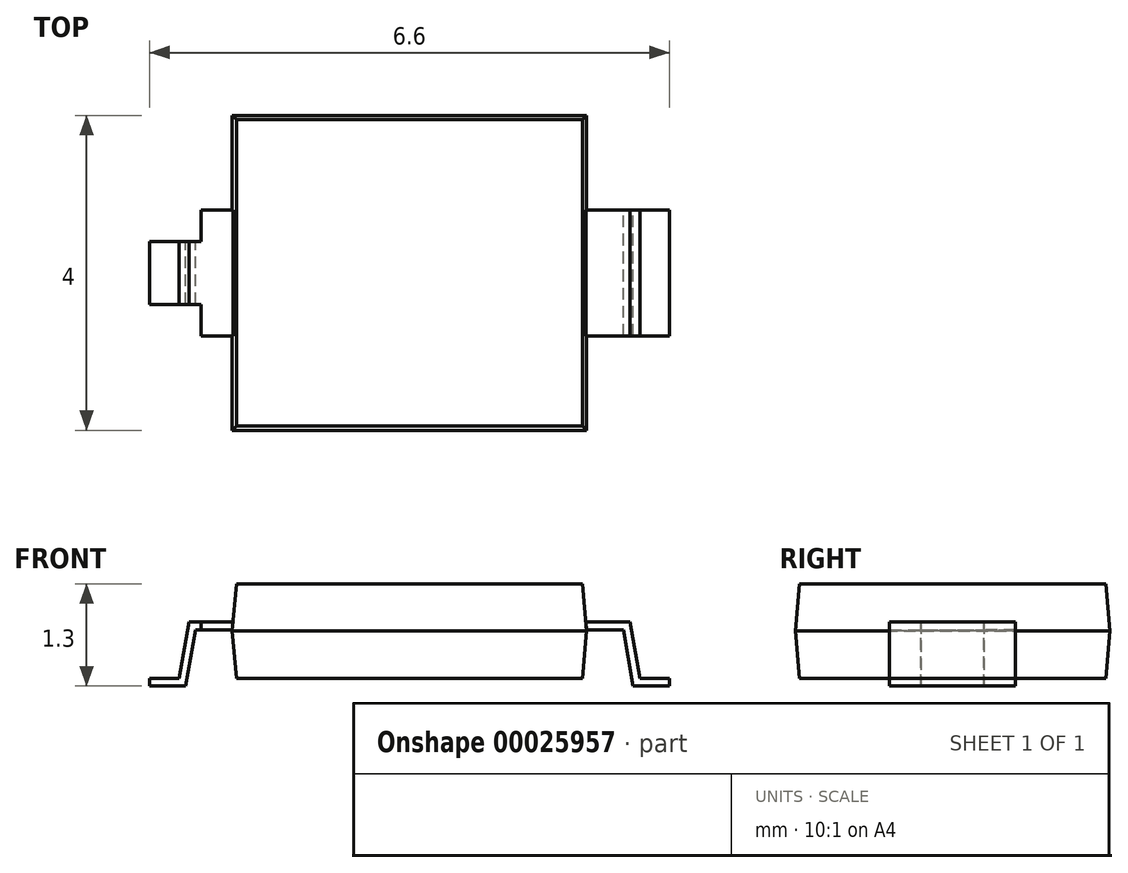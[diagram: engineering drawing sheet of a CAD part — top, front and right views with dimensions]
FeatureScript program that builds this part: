
annotation { "Feature Type Name" : "Feature", "Feature Type Description" : "" }
export const myFeature = defineFeature(function(context is Context, id is Id, definition is map)
    precondition{}
    {
        {
            var Q0;
            Q0=qCreatedBy(makeId("Top.planeOp"),FACE);
            var sketch = newSketch(context, id + "F0", { "sketchPlane" : qUnion([Q0])});
            skLineSegment(sketch, "E0.rect.bottom", {"start": v(2.25, -2) * mm, "end": v(-2.25, -2) * mm});
            skLineSegment(sketch, "E0.rect.top", {"start": v(2.25, 2) * mm, "end": v(-2.25, 2) * mm});
            skLineSegment(sketch, "E0.rect.left", {"start": v(2.25, -2) * mm, "end": v(2.25, 2) * mm});
            skLineSegment(sketch, "E0.rect.right", {"start": v(-2.25, -2) * mm, "end": v(-2.25, 2) * mm});
            skPoint(sketch, "E0.rect.middle", {"position": v(0, 0) * mm});
            skSolve(sketch);
        }
        {
            var Q0;
            Q0 = qSketchRegion(id + "F0", true);
            extrude(context, id + "F1", {"entities" : qUnion([Q0]), "endBound" : BoundingType.SYMMETRIC, "depth" : 1.2 * mm, "hasDraft" : true, "draftAngle" : 5 * degree, "draftPullDirection" : true});
        }
        {
            var Q0;
            Q0=qCreatedBy(makeId("Front.planeOp"),FACE);
            var sketch = newSketch(context, id + "F2", { "sketchPlane" : qUnion([Q0])});
            skLineSegment(sketch, "E1", {"start": v(-2.24, 0.11) * mm, "end": v(-2.8, 0.11) * mm});
            skLineSegment(sketch, "E2", {"start": v(-2.8, 0.11) * mm, "end": v(-2.93, -0.6) * mm});
            skLineSegment(sketch, "E3", {"start": v(-2.93, -0.6) * mm, "end": v(-3.3, -0.6) * mm});
            skLineSegment(sketch, "E4", {"start": v(-3.3, -0.6) * mm, "end": v(-3.3, -0.7) * mm});
            skLineSegment(sketch, "E5", {"start": v(-3.3, -0.7) * mm, "end": v(-2.84, -0.7) * mm});
            skLineSegment(sketch, "E6", {"start": v(-2.84, -0.7) * mm, "end": v(-2.72, 0.01) * mm});
            skLineSegment(sketch, "E7", {"start": v(-2.72, 0.01) * mm, "end": v(-2.25, 0.01) * mm});
            skLineSegment(sketch, "E8", {"start": v(0, 0) * mm, "end": v(0, -2.3) * mm, "construction": true});
            skLineSegment(sketch, "E9", {"start": v(-2.25, 0.01) * mm, "end": v(-2.24, 0.11) * mm});
            skLineSegment(sketch, "E10.MirrorCS", {"start": v(3.3, -0.6) * mm, "end": v(3.3, -0.7) * mm});
            skLineSegment(sketch, "E11.MirrorCS", {"start": v(2.25, 0.01) * mm, "end": v(2.24, 0.11) * mm});
            skLineSegment(sketch, "E12.MirrorCS", {"start": v(2.24, 0.11) * mm, "end": v(2.8, 0.11) * mm});
            skLineSegment(sketch, "E13.MirrorCS", {"start": v(2.93, -0.6) * mm, "end": v(3.3, -0.6) * mm});
            skLineSegment(sketch, "E14.MirrorCS", {"start": v(2.8, 0.11) * mm, "end": v(2.93, -0.6) * mm});
            skLineSegment(sketch, "E15.MirrorCS", {"start": v(3.3, -0.7) * mm, "end": v(2.84, -0.7) * mm});
            skLineSegment(sketch, "E16.MirrorCS", {"start": v(2.84, -0.7) * mm, "end": v(2.72, 0.01) * mm});
            skLineSegment(sketch, "E17.MirrorCS", {"start": v(2.72, 0.01) * mm, "end": v(2.25, 0.01) * mm});
            skSolve(sketch);
        }
        {
            var Q0;
            Q0 = qSketchRegion(id + "F2", true);
            extrude(context, id + "F3", {"entities" : qUnion([Q0]), "endBound" : BoundingType.SYMMETRIC, "depth" : 1.6 * mm});
        }
        {
            var Q0;
            Q0=makeQuery(id+"F3.opExtrude","SWEPT_FACE",FACE,{"disambiguationData":[OSD([sQuery(id+"F2.wireOp",EDGE,"E1")])]});
            var sketch = newSketch(context, id + "F4", { "sketchPlane" : qUnion([Q0])});
            skLineSegment(sketch, "E18.bottom", {"start": v(-3.46, 0.9) * mm, "end": v(-2.65, 0.9) * mm});
            skLineSegment(sketch, "E18.top", {"start": v(-3.46, 0.4) * mm, "end": v(-2.65, 0.4) * mm});
            skLineSegment(sketch, "E18.left", {"start": v(-3.46, 0.9) * mm, "end": v(-3.46, 0.4) * mm});
            skLineSegment(sketch, "E18.right", {"start": v(-2.65, 0.9) * mm, "end": v(-2.65, 0.4) * mm});
            skLineSegment(sketch, "E19.MirrorCS", {"start": v(-3.46, -0.4) * mm, "end": v(-2.65, -0.4) * mm});
            skLineSegment(sketch, "E20.MirrorCS", {"start": v(-3.46, -0.9) * mm, "end": v(-3.46, -0.4) * mm});
            skLineSegment(sketch, "E21.MirrorCS", {"start": v(-3.46, -0.9) * mm, "end": v(-2.65, -0.9) * mm});
            skLineSegment(sketch, "E22.MirrorCS", {"start": v(-2.65, -0.9) * mm, "end": v(-2.65, -0.4) * mm});
            skSolve(sketch);
        }
        {
            var Q0;
            Q0 = qSketchRegion(id + "F4", true);
            var Q1;
            Q1=makeQuery(id+"F3.opExtrude","SWEPT_FACE",FACE,{"disambiguationData":[OSD([sQuery(id+"F2.wireOp",EDGE,"E5")])]});
            extrude(context, id + "F5", {"entities" : qUnion([Q0]), "operationType" : NewBodyOperationType.REMOVE, "endBound" : BoundingType.UP_TO_SURFACE, "oppositeDirection" : true, "endBoundEntityFace" : qUnion([Q1]), "depth" : 25 * mm});
        }
    });
